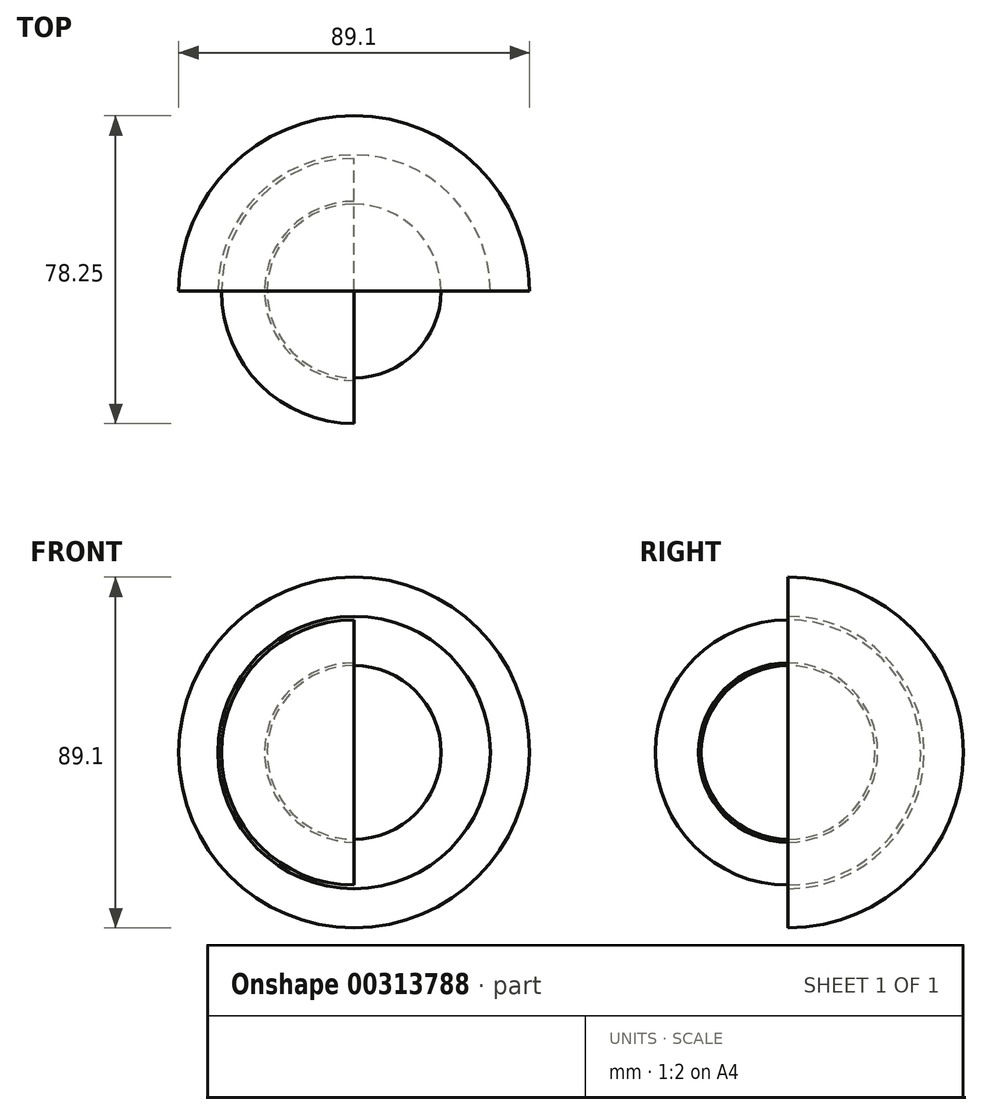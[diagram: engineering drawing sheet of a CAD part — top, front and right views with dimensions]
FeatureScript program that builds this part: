
annotation { "Feature Type Name" : "Feature", "Feature Type Description" : "" }
export const myFeature = defineFeature(function(context is Context, id is Id, definition is map)
    precondition{}
    {
        {
            var Q0;
            Q0=qCreatedBy(makeId("Front.planeOp"),FACE);
            var sketch = newSketch(context, id + "F0", { "sketchPlane" : qUnion([Q0])});
            skCircle(sketch, "E0", {"center": v(0, 0) * mm, "radius": 22.79 * mm});
            skCircle(sketch, "E1", {"center": v(0, 0) * mm, "radius": 33.7 * mm});
            skLineSegment(sketch, "E2", {"start": v(0, 33.7) * mm, "end": v(0, -33.7) * mm});
            skSolve(sketch);
        }
        {
            var Q0;
            {var subQ0=sQuery(id+"F0.wireOp",EDGE,"E2");var subQ1=sQuery(id+"F0.wireOp",EDGE,"E0");var subQ2=makeQuery(id+"F0.imprint","INTERSECT",VERTEX,{"disambiguationData":[OD(0.0)],"derivedFrom":[subQ1,subQ0]});Q0=makeQuery(id+"F0.imprint","IMPRINT",FACE,{"disambiguationData":[TD([[makeQuery(id+"F0.imprint","IMPRINT",EDGE,{"disambiguationData":[TD([[subQ2,-1.0]])],"derivedFrom":subQ1}),-1.0]])]});}
            var Q1;
            Q1=sQuery(id+"F0.wireOp",EDGE,"E2");
            revolve(context, id + "F1", {"entities" : qUnion([Q0]), "axis" : qUnion([Q1]), "revolveType" : RevolveType.SYMMETRIC, "angle" : 180 * degree});
        }
        {
            var Q0;
            Q0=qCreatedBy(makeId("Right.planeOp"),FACE);
            var sketch = newSketch(context, id + "F2", { "sketchPlane" : qUnion([Q0])});
            skCircle(sketch, "E3", {"center": v(0, 0) * mm, "radius": 22.08 * mm});
            skLineSegment(sketch, "E4", {"start": v(0, 52.22) * mm, "end": v(0, -60.9) * mm});
            skSolve(sketch);
        }
        {
            var Q0;
            {var subQ0=sQuery(id+"F2.wireOp",EDGE,"E4");var subQ1=sQuery(id+"F2.wireOp",EDGE,"E3");var subQ2=makeQuery(id+"F2.imprint","INTERSECT",VERTEX,{"disambiguationData":[OD(0.0)],"derivedFrom":[subQ1,subQ0]});Q0=makeQuery(id+"F2.imprint","IMPRINT",FACE,{"disambiguationData":[TD([[makeQuery(id+"F2.imprint","IMPRINT",EDGE,{"disambiguationData":[TD([[subQ2,1.0]])],"derivedFrom":subQ1}),1.0]])]});}
            var Q1;
            Q1=sQuery(id+"F2.wireOp",EDGE,"E4");
            revolve(context, id + "F3", {"entities" : qUnion([Q0]), "axis" : qUnion([Q1]), "revolveType" : RevolveType.FULL});
        }
        {
            var Q0;
            Q0=qCreatedBy(makeId("Front.planeOp"),FACE);
            var sketch = newSketch(context, id + "F4", { "sketchPlane" : qUnion([Q0])});
            skCircle(sketch, "E5", {"center": v(0, 0) * mm, "radius": 34.6 * mm});
            skCircle(sketch, "E6", {"center": v(0, 0) * mm, "radius": 44.55 * mm});
            skLineSegment(sketch, "E7", {"start": v(0, 57.54) * mm, "end": v(0, -49.86) * mm});
            skSolve(sketch);
        }
        {
            var Q0;
            {var subQ0=sQuery(id+"F4.wireOp",EDGE,"E7");var subQ1=sQuery(id+"F4.wireOp",EDGE,"E5");var subQ2=makeQuery(id+"F4.imprint","INTERSECT",VERTEX,{"disambiguationData":[OD(0.0)],"derivedFrom":[subQ1,subQ0]});Q0=makeQuery(id+"F4.imprint","IMPRINT",FACE,{"disambiguationData":[TD([[makeQuery(id+"F4.imprint","IMPRINT",EDGE,{"disambiguationData":[TD([[subQ2,-1.0]])],"derivedFrom":subQ1}),-1.0]])]});}
            var Q1;
            Q1=sQuery(id+"F4.wireOp",EDGE,"E7");
            revolve(context, id + "F5", {"entities" : qUnion([Q0]), "axis" : qUnion([Q1]), "revolveType" : RevolveType.ONE_DIRECTION, "angle" : 180 * degree});
        }
    });
